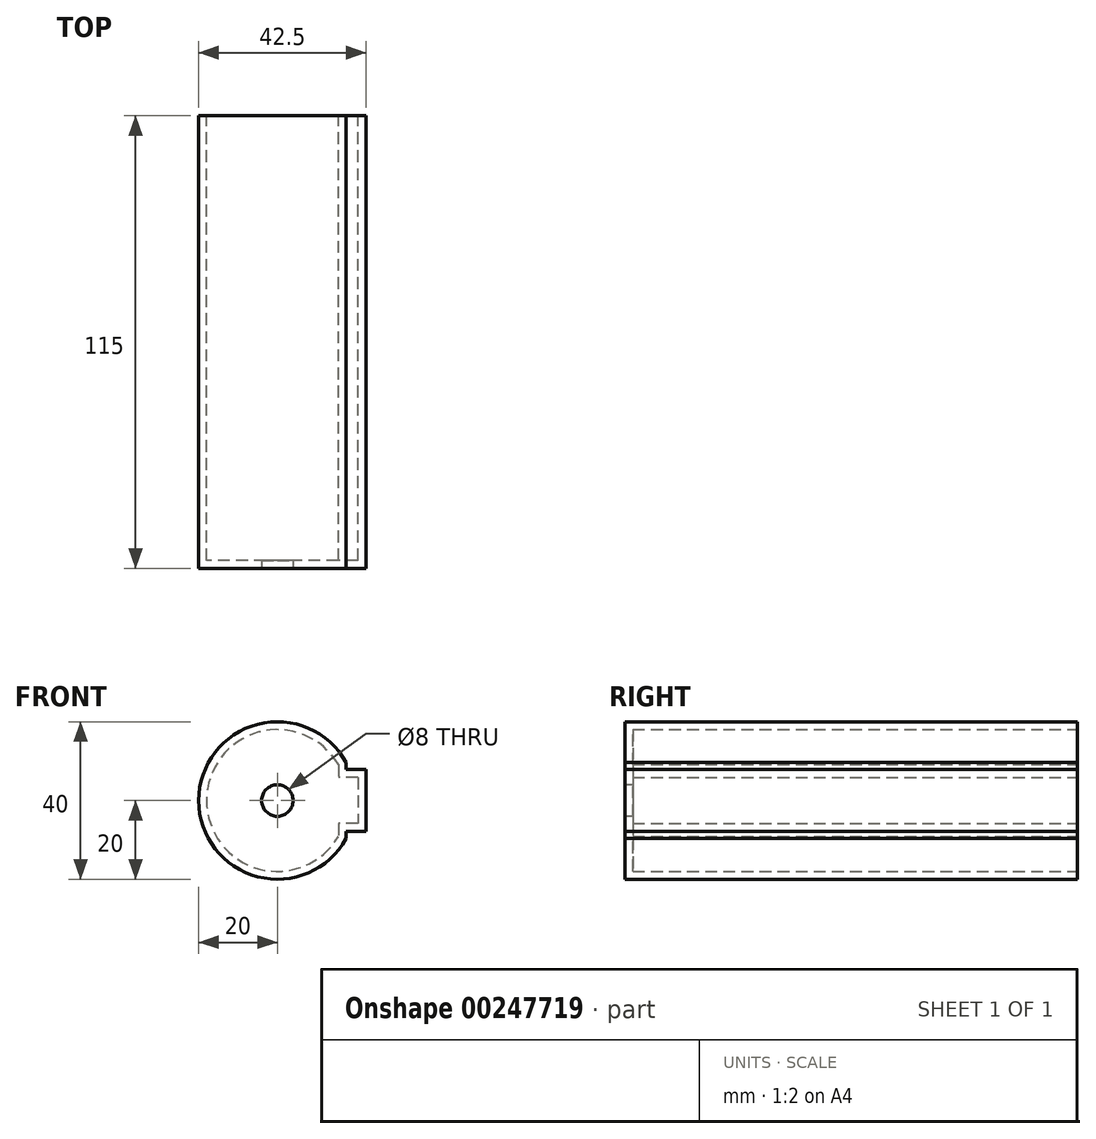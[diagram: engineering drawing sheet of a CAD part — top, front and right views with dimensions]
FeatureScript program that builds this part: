
annotation { "Feature Type Name" : "Feature", "Feature Type Description" : "" }
export const myFeature = defineFeature(function(context is Context, id is Id, definition is map)
    precondition{}
    {
        {
            var Q0;
            Q0=qCreatedBy(makeId("Front.planeOp"),FACE);
            var sketch = newSketch(context, id + "F0", { "sketchPlane" : qUnion([Q0])});
            skArc(sketch, "E0", {"start": v(17.5, 9.68) * mm, "mid": v(-20, 0) * mm, "end": v(17.5, -9.68) * mm});
            skPoint(sketch, "E1", {"position": v(20, 0) * mm});
            skLineSegment(sketch, "E2.bottom", {"start": v(22.5, 7.84) * mm, "end": v(17.5, 7.84) * mm});
            skLineSegment(sketch, "E2.top", {"start": v(22.5, -7.84) * mm, "end": v(17.5, -7.84) * mm});
            skLineSegment(sketch, "E2.left", {"start": v(22.5, 7.84) * mm, "end": v(22.5, -7.84) * mm});
            skLineSegment(sketch, "E2.right", {"start": v(17.5, 9.68) * mm, "end": v(17.5, 7.84) * mm});
            skLineSegment(sketch, "E3.trimOffspring", {"start": v(17.5, -7.84) * mm, "end": v(17.5, -9.68) * mm});
            skSolve(sketch);
        }
        {
            var Q0;
            Q0 = qSketchRegion(id + "F0", true);
            extrude(context, id + "F1", {"entities" : qUnion([Q0]), "depth" : 115 * mm, "symmetric" : true});
        }
        {
            var Q0;
            Q0=makeQuery(id+"F1.opExtrude","CAP_FACE",FACE,{"disambiguationData":[OSD([sQuery(id+"F0.wireOp",EDGE,"E0"),sQuery(id+"F0.wireOp",EDGE,"E2.bottom"),sQuery(id+"F0.wireOp",EDGE,"E2.top"),sQuery(id+"F0.wireOp",EDGE,"E2.left"),sQuery(id+"F0.wireOp",EDGE,"E2.right"),sQuery(id+"F0.wireOp",EDGE,"E3.trimOffspring")])],"isStart":true});
            shell(context, id + "F2", {"entities" : qUnion([Q0]), "thickness" : 2 * mm});
        }
        {
            var Q0;
            Q0=makeQuery(id+"F1.opExtrude","CAP_FACE",FACE,{"disambiguationData":[OSD([sQuery(id+"F0.wireOp",EDGE,"E0"),sQuery(id+"F0.wireOp",EDGE,"E2.bottom"),sQuery(id+"F0.wireOp",EDGE,"E2.top"),sQuery(id+"F0.wireOp",EDGE,"E2.left"),sQuery(id+"F0.wireOp",EDGE,"E2.right"),sQuery(id+"F0.wireOp",EDGE,"E3.trimOffspring")])],"isStart":false});
            var sketch = newSketch(context, id + "F3", { "sketchPlane" : qUnion([Q0])});
            skCircle(sketch, "E4", {"center": v(0, 0) * mm, "radius": 4 * mm});
            skSolve(sketch);
        }
        {
            var Q0;
            Q0 = qSketchRegion(id + "F3", true);
            extrude(context, id + "F4", {"entities" : qUnion([Q0]), "operationType" : NewBodyOperationType.REMOVE, "oppositeDirection" : true, "depth" : 25 * mm});
        }
    });
